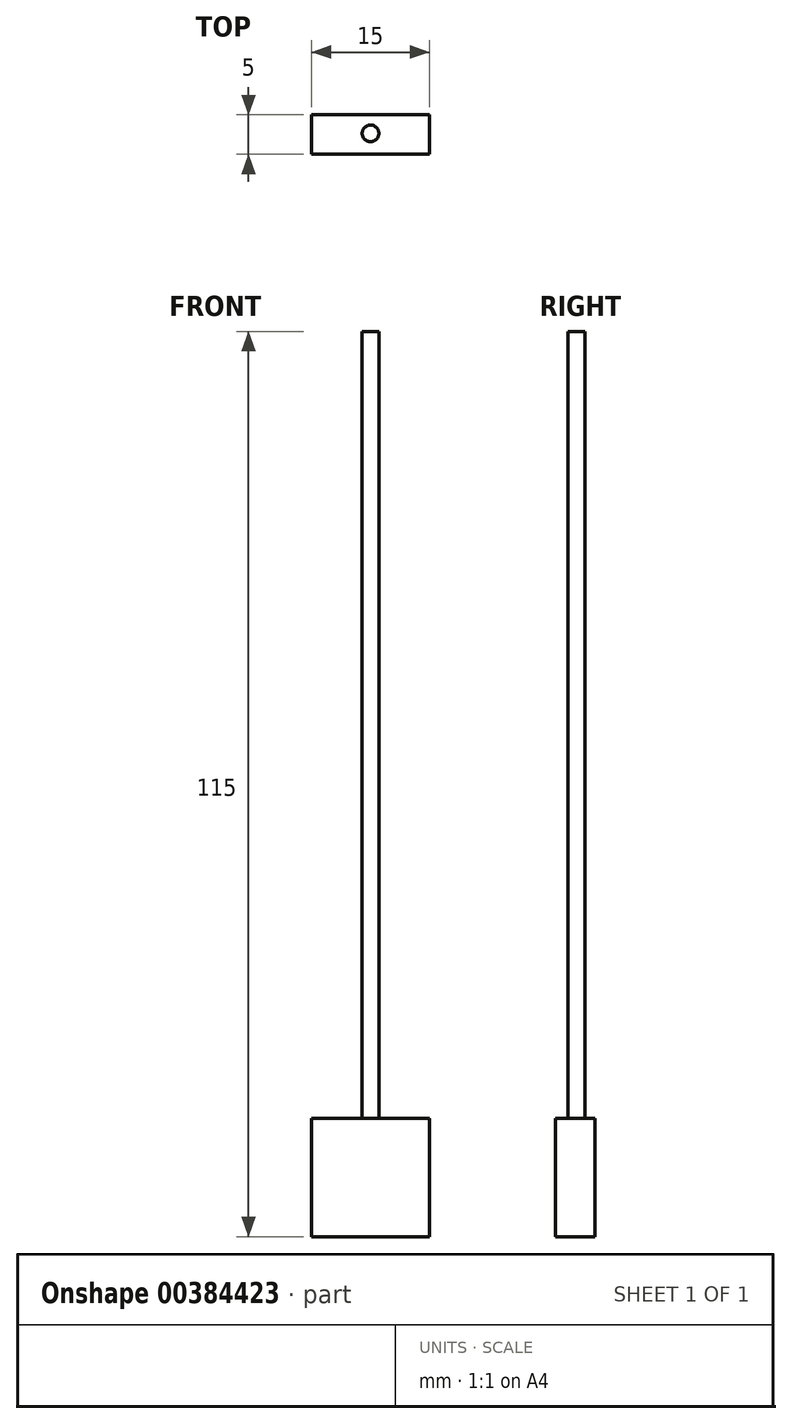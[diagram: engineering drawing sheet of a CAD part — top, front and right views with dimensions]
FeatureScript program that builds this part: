
annotation { "Feature Type Name" : "Feature", "Feature Type Description" : "" }
export const myFeature = defineFeature(function(context is Context, id is Id, definition is map)
    precondition{}
    {
        {
            var Q0;
            Q0=qCreatedBy(makeId("Front.planeOp"),FACE);
            var sketch = newSketch(context, id + "F0", { "sketchPlane" : qUnion([Q0])});
            skLineSegment(sketch, "E0.bottom", {"start": v(7.5, 7.5) * mm, "end": v(-7.5, 7.5) * mm});
            skLineSegment(sketch, "E0.top", {"start": v(7.5, -7.5) * mm, "end": v(-7.5, -7.5) * mm});
            skLineSegment(sketch, "E0.left", {"start": v(7.5, 7.5) * mm, "end": v(7.5, -7.5) * mm});
            skLineSegment(sketch, "E0.right", {"start": v(-7.5, 7.5) * mm, "end": v(-7.5, -7.5) * mm});
            skPoint(sketch, "E0.middle", {"position": v(0, 0) * mm});
            skSolve(sketch);
        }
        {
            var Q0;
            Q0=makeQuery(id+"F0.imprint","IMPRINT",FACE,{"disambiguationData":[TD([[makeQuery(id+"F0.imprint","IMPRINT",EDGE,{"derivedFrom":sQuery(id+"F0.wireOp",EDGE,"E0.bottom")}),1.0]])]});
            extrude(context, id + "F1", {"entities" : qUnion([Q0]), "depth" : 5 * mm});
        }
        {
            var Q0;
            Q0=makeQuery(id+"F1.opExtrude","SWEPT_FACE",FACE,{"disambiguationData":[OSD([sQuery(id+"F0.wireOp",EDGE,"E0.bottom")])]});
            var sketch = newSketch(context, id + "F2", { "sketchPlane" : qUnion([Q0])});
            skCircle(sketch, "E1", {"center": v(0, -2.35) * mm, "radius": 1.06 * mm});
            skPoint(sketch, "E1.centerSnap0", {"position": v(0, 0) * mm});
            skSolve(sketch);
        }
        {
            var Q0;
            Q0=makeQuery(id+"F2.imprint","IMPRINT",FACE,{"disambiguationData":[TD([[makeQuery(id+"F2.imprint","IMPRINT",EDGE,{"derivedFrom":sQuery(id+"F2.wireOp",EDGE,"E1")}),1.0]])]});
            extrude(context, id + "F3", {"entities" : qUnion([Q0]), "operationType" : NewBodyOperationType.ADD, "depth" : 100 * mm});
        }
    });
